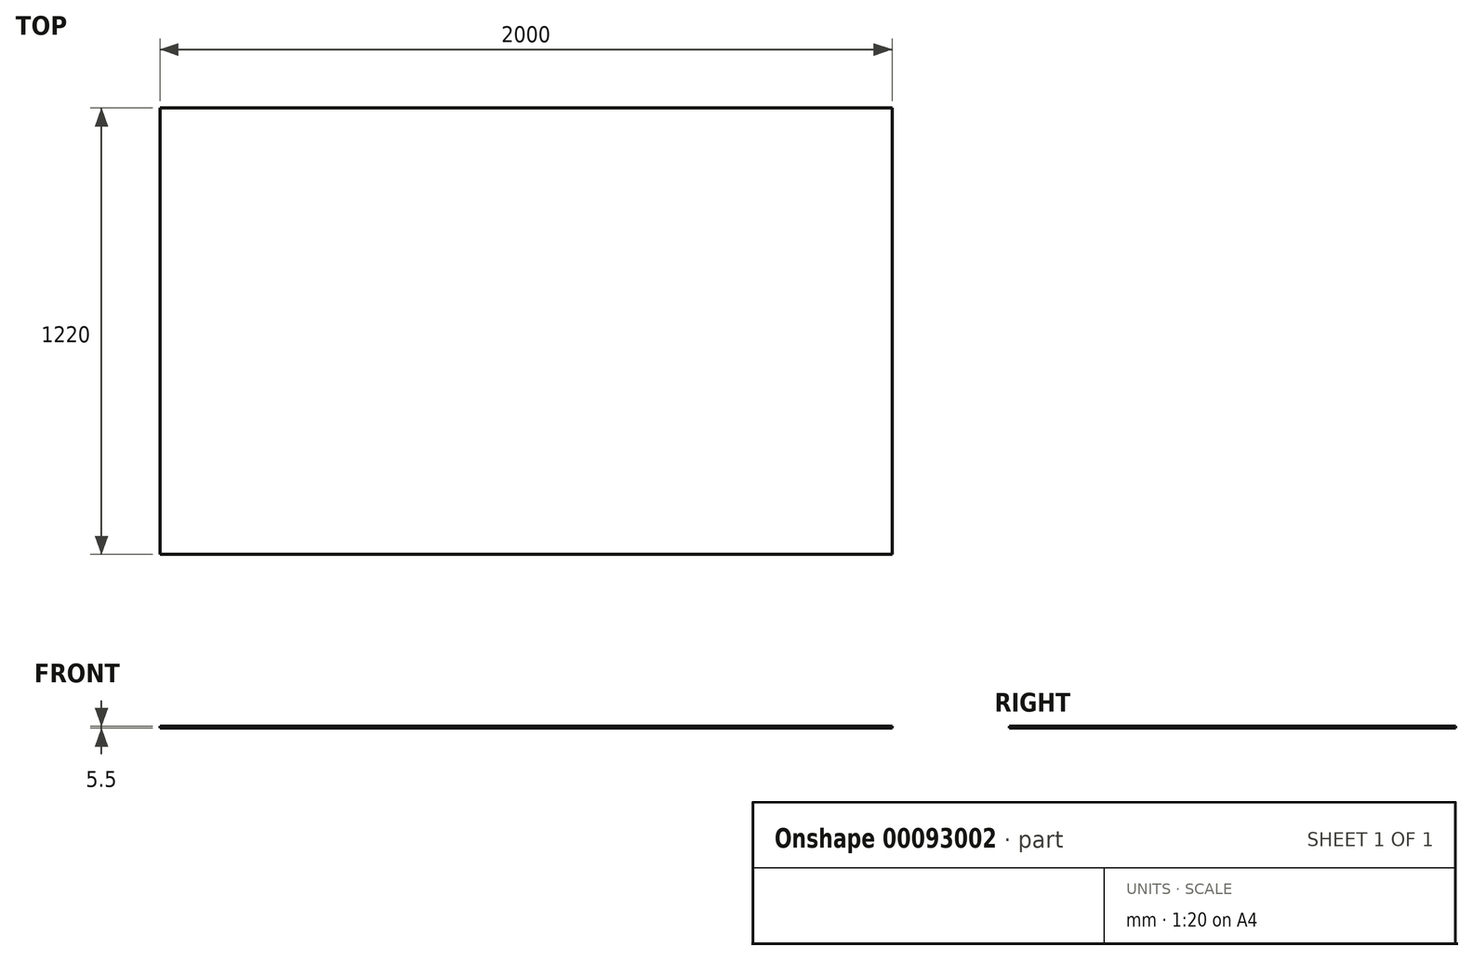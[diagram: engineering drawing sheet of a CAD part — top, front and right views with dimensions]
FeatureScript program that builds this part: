
annotation { "Feature Type Name" : "Feature", "Feature Type Description" : "" }
export const myFeature = defineFeature(function(context is Context, id is Id, definition is map)
    precondition{}
    {
        {
            var Q0;
            Q0=qCreatedBy(makeId("Top.planeOp"),FACE);
            var sketch = newSketch(context, id + "F0", { "sketchPlane" : qUnion([Q0])});
            skLineSegment(sketch, "E0.bottom", {"start": v(0, 0) * mm, "end": v(2000, 0) * mm});
            skLineSegment(sketch, "E0.top", {"start": v(0, 1220) * mm, "end": v(2000, 1220) * mm});
            skLineSegment(sketch, "E0.left", {"start": v(0, 0) * mm, "end": v(0, 1220) * mm});
            skLineSegment(sketch, "E0.right", {"start": v(2000, 0) * mm, "end": v(2000, 1220) * mm});
            skSolve(sketch);
        }
        {
            var Q0;
            Q0=makeQuery(id+"F0.imprint","IMPRINT",FACE,{"disambiguationData":[TD([[makeQuery(id+"F0.imprint","IMPRINT",EDGE,{"derivedFrom":sQuery(id+"F0.wireOp",EDGE,"E0.bottom")}),1.0]])]});
            extrude(context, id + "F1", {"entities" : qUnion([Q0]), "depth" : 5.5 * mm});
        }
    });
